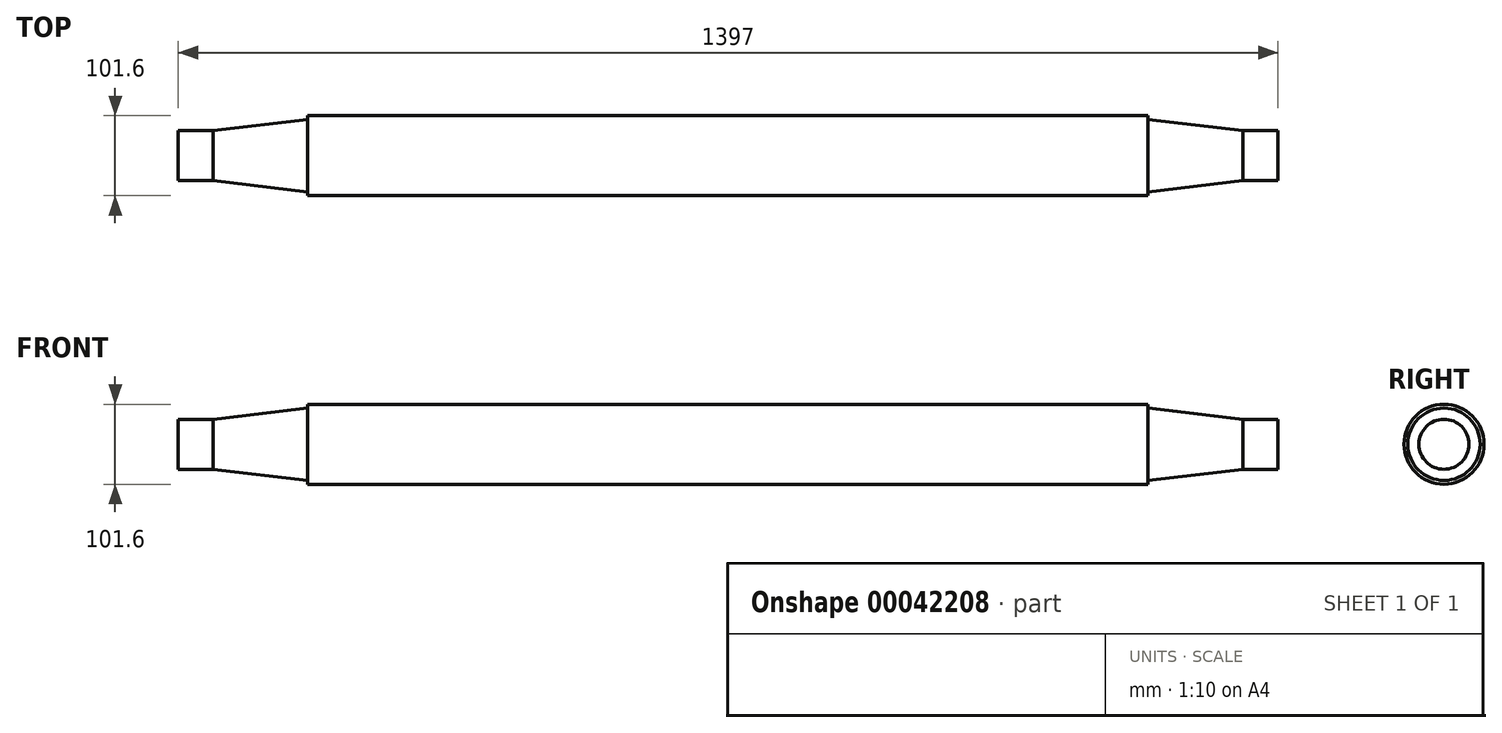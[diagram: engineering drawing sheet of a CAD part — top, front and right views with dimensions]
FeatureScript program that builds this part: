
annotation { "Feature Type Name" : "Feature", "Feature Type Description" : "" }
export const myFeature = defineFeature(function(context is Context, id is Id, definition is map)
    precondition{}
    {
        {
            var Q0;
            Q0=qCreatedBy(makeId("Front.planeOp"),FACE);
            var sketch = newSketch(context, id + "F0", { "sketchPlane" : qUnion([Q0])});
            skLineSegment(sketch, "E0", {"start": v(-698.5, 0) * mm, "end": v(698.5, 0) * mm});
            skLineSegment(sketch, "E1.0", {"start": v(-533.97, 50.8) * mm, "end": v(533.4, 50.8) * mm});
            skLineSegment(sketch, "E2.0", {"start": v(-698.5, 31.75) * mm, "end": v(-654.05, 31.75) * mm});
            skLineSegment(sketch, "E3", {"start": v(-698.5, 31.75) * mm, "end": v(-698.5, 0) * mm});
            skLineSegment(sketch, "E4", {"start": v(-533.4, 45.97) * mm, "end": v(-654.05, 31.75) * mm});
            skLineSegment(sketch, "E5", {"start": v(-533.4, 45.97) * mm, "end": v(-533.97, 50.8) * mm});
            skLineSegment(sketch, "E6", {"start": v(0, 0) * mm, "end": v(0, -221) * mm, "construction": true});
            skLineSegment(sketch, "E7.MirrorCS", {"start": v(698.5, 31.75) * mm, "end": v(698.5, 0) * mm});
            skLineSegment(sketch, "E8.MirrorCS", {"start": v(698.5, 31.75) * mm, "end": v(654.05, 31.75) * mm});
            skLineSegment(sketch, "E9.MirrorCS", {"start": v(533.4, 45.97) * mm, "end": v(654.05, 31.75) * mm});
            skLineSegment(sketch, "E10", {"start": v(533.4, 45.97) * mm, "end": v(533.4, 50.8) * mm});
            skSolve(sketch);
        }
        {
            var Q0;
            Q0=qSketchRegion(id+"F0",true);
            var Q1;
            Q1=sQuery(id+"F0.wireOp",EDGE,"E0");
            revolve(context, id + "F1", {"entities" : qUnion([Q0]), "axis" : qUnion([Q1]), "revolveType" : RevolveType.FULL});
        }
    });
